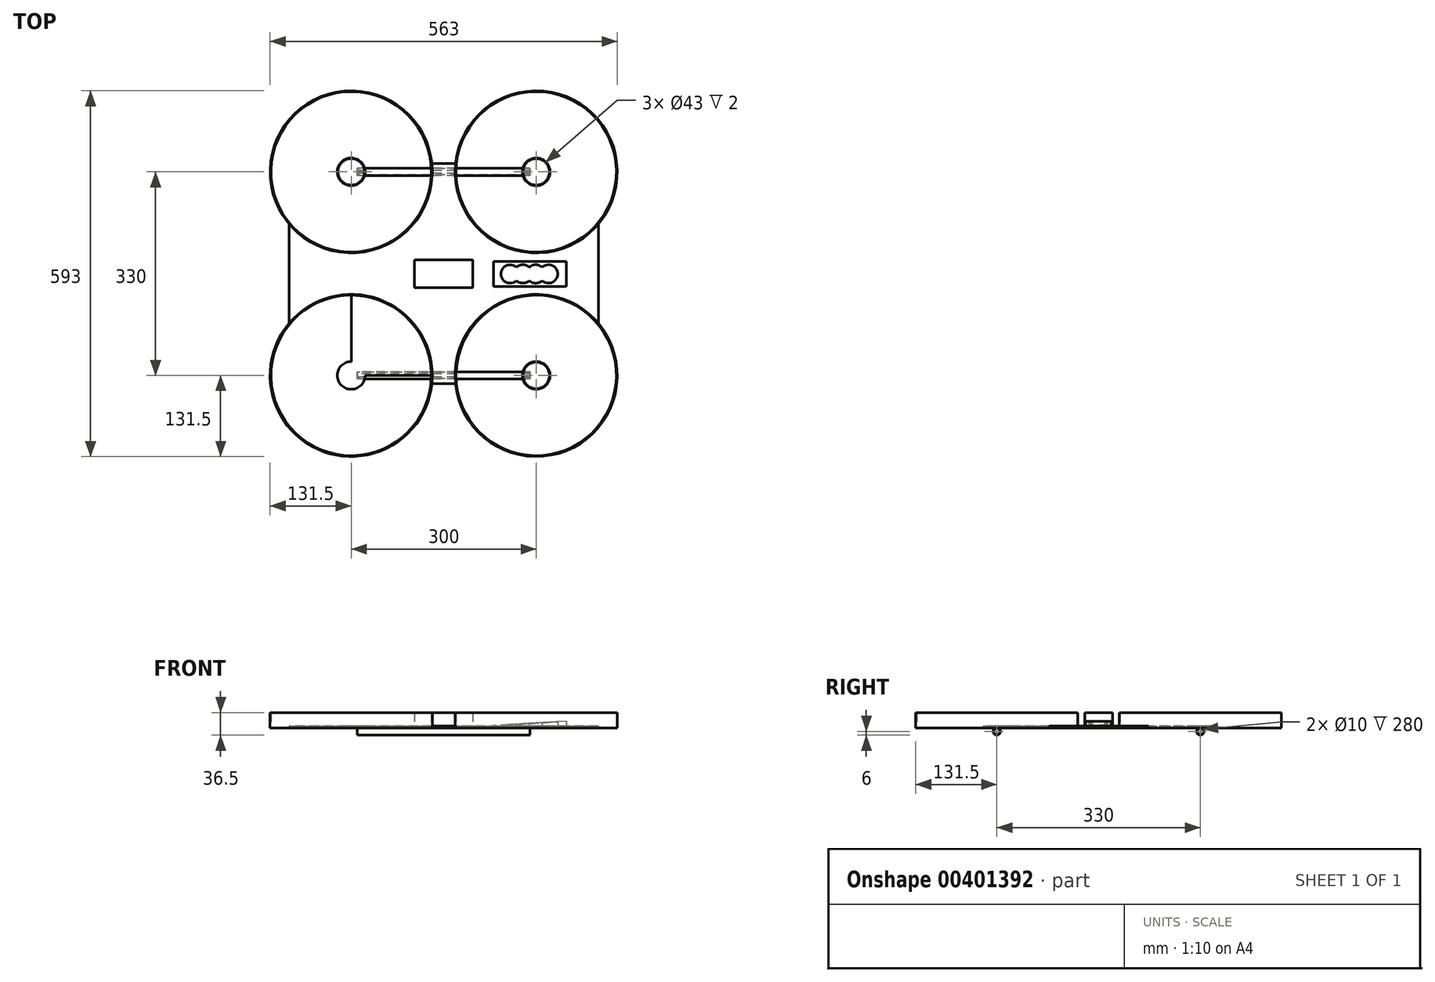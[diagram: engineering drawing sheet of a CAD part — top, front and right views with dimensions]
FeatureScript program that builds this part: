
annotation { "Feature Type Name" : "Feature", "Feature Type Description" : "" }
export const myFeature = defineFeature(function(context is Context, id is Id, definition is map)
    precondition{}
    {
        {
            var Q0;
            Q0=qCreatedBy(makeId("Top.planeOp"),FACE);
            var sketch = newSketch(context, id + "F0", { "sketchPlane" : qUnion([Q0])});
            skLineSegment(sketch, "E0.bottom", {"start": v(127.5, 165) * mm, "end": v(20, 165) * mm});
            skLineSegment(sketch, "E0.top", {"start": v(127.5, -165) * mm, "end": v(20, -165) * mm});
            skLineSegment(sketch, "E0.left", {"start": v(150, 142.5) * mm, "end": v(150, 35) * mm});
            skLineSegment(sketch, "E0.right", {"start": v(-150, 142.5) * mm, "end": v(-150, 35) * mm});
            skPoint(sketch, "E0.middle", {"position": v(0, 0) * mm});
            skArc(sketch, "E1", {"start": v(-277.12, 131.33) * mm, "mid": v(-136.22, 34.22) * mm, "end": v(-18.66, 158.56) * mm});
            skArc(sketch, "E2", {"start": v(-130.96, -295.11) * mm, "mid": v(-18.85, -155.46) * mm, "end": v(-150, -33.5) * mm});
            skArc(sketch, "E3", {"start": v(150, -33.5) * mm, "mid": v(140.46, -33.85) * mm, "end": v(130.96, -34.89) * mm});
            skArc(sketch, "E4", {"start": v(18.63, 159.26) * mm, "mid": v(135.88, 34.26) * mm, "end": v(277.12, 131.33) * mm});
            skArc(sketch, "E5", {"start": v(-150, 35) * mm, "mid": v(-60.39, 70.82) * mm, "end": v(-20.16, 158.55) * mm});
            skArc(sketch, "E6", {"start": v(-20.17, -158.32) * mm, "mid": v(-60.47, -70.74) * mm, "end": v(-150, -35) * mm});
            skArc(sketch, "E7", {"start": v(150, -35) * mm, "mid": v(60.47, -70.74) * mm, "end": v(20.17, -158.32) * mm});
            skArc(sketch, "E8", {"start": v(20.12, 159.3) * mm, "mid": v(60.11, 71.09) * mm, "end": v(150, 35) * mm});
            skArc(sketch, "E9", {"start": v(-127.5, 165) * mm, "mid": v(-165.9, 180.9) * mm, "end": v(-150, 142.5) * mm});
            skArc(sketch, "E10", {"start": v(172.44, 163.38) * mm, "mid": v(134.67, 181.47) * mm, "end": v(150, 142.5) * mm});
            skArc(sketch, "E11", {"start": v(150, -142.5) * mm, "mid": v(138.1, -184.1) * mm, "end": v(170.2, -155.1) * mm});
            skArc(sketch, "E12", {"start": v(-170.2, -155.1) * mm, "mid": v(-138.1, -184.1) * mm, "end": v(-150, -142.5) * mm});
            skPoint(sketch, "E13.orphan", {"position": v(-150, 179.73) * mm});
            skPoint(sketch, "E14.orphan", {"position": v(-171.77, 150.07) * mm});
            skArc(sketch, "E15.trimOffspring", {"start": v(-150, 33.5) * mm, "mid": v(-140.46, 33.85) * mm, "end": v(-130.96, 34.89) * mm});
            skLineSegment(sketch, "E16.trimOffspring", {"start": v(-150, 33.5) * mm, "end": v(-150, -33.5) * mm});
            skArc(sketch, "E17.trimOffspring", {"start": v(-150, 142.5) * mm, "mid": v(-141.54, 185.85) * mm, "end": v(-165.68, 148.86) * mm});
            skArc(sketch, "E18.trimOffspring", {"start": v(-20, 165) * mm, "mid": v(-241.92, 256.92) * mm, "end": v(-150, 35) * mm});
            skArc(sketch, "E19.trimOffspring", {"start": v(-18.5, 165) * mm, "mid": v(-242.98, 257.98) * mm, "end": v(-150, 33.5) * mm});
            skLineSegment(sketch, "E20.trimOffspring", {"start": v(-20, 165) * mm, "end": v(-127.5, 165) * mm});
            skLineSegment(sketch, "E21.trimOffspring", {"start": v(18.5, 165) * mm, "end": v(-18.5, 165) * mm});
            skPoint(sketch, "E22.orphan", {"position": v(150, 155.34) * mm});
            skArc(sketch, "E23.trimOffspring", {"start": v(150, 142.5) * mm, "mid": v(165.9, 180.9) * mm, "end": v(127.5, 165) * mm});
            skPoint(sketch, "E24.orphan", {"position": v(172.08, 149.08) * mm});
            skArc(sketch, "E25.trimOffspring", {"start": v(150, 35) * mm, "mid": v(241.92, 256.92) * mm, "end": v(20, 165) * mm});
            skArc(sketch, "E26.trimOffspring", {"start": v(150, 33.5) * mm, "mid": v(242.98, 257.98) * mm, "end": v(18.5, 165) * mm});
            skLineSegment(sketch, "E27.trimOffspring", {"start": v(150, 33.5) * mm, "end": v(150, -33.5) * mm});
            skLineSegment(sketch, "E28.trimOffspring", {"start": v(150, -35) * mm, "end": v(150, -142.5) * mm});
            skPoint(sketch, "E29.orphan", {"position": v(150, -179.73) * mm});
            skArc(sketch, "E30.trimOffspring", {"start": v(127.5, -165) * mm, "mid": v(165.9, -180.9) * mm, "end": v(150, -142.5) * mm});
            skPoint(sketch, "E31.orphan", {"position": v(171.77, -150.07) * mm});
            skArc(sketch, "E32.trimOffspring", {"start": v(277.12, -131.33) * mm, "mid": v(136.34, -34.21) * mm, "end": v(18.67, -158.33) * mm});
            skPoint(sketch, "E33.orphan", {"position": v(-171.77, -150.07) * mm});
            skArc(sketch, "E34.trimOffspring", {"start": v(130.97, 34.88) * mm, "mid": v(140.46, 33.85) * mm, "end": v(150, 33.5) * mm});
            skArc(sketch, "E35.trimOffspring", {"start": v(20, -165) * mm, "mid": v(241.92, -256.92) * mm, "end": v(150, -35) * mm});
            skLineSegment(sketch, "E36.trimOffspring", {"start": v(18.5, -165) * mm, "end": v(-18.5, -165) * mm});
            skArc(sketch, "E37.trimOffspring", {"start": v(18.5, -165) * mm, "mid": v(242.98, -257.98) * mm, "end": v(150, -33.5) * mm});
            skArc(sketch, "E38.trimOffspring", {"start": v(-18.67, -158.33) * mm, "mid": v(-136.34, -34.21) * mm, "end": v(-277.12, -131.33) * mm});
            skLineSegment(sketch, "E39.trimOffspring", {"start": v(-20, -165) * mm, "end": v(-127.5, -165) * mm});
            skPoint(sketch, "E40.orphan", {"position": v(-150, -155.34) * mm});
            skArc(sketch, "E41.trimOffspring", {"start": v(-150, -142.5) * mm, "mid": v(-165.9, -180.9) * mm, "end": v(-127.5, -165) * mm});
            skArc(sketch, "E42.trimOffspring", {"start": v(-150, -35) * mm, "mid": v(-241.92, -256.92) * mm, "end": v(-20, -165) * mm});
            skArc(sketch, "E43.trimOffspring", {"start": v(-150, -33.5) * mm, "mid": v(-242.98, -257.98) * mm, "end": v(-18.5, -165) * mm});
            skLineSegment(sketch, "E44.trimOffspring", {"start": v(-150, -35) * mm, "end": v(-150, -142.5) * mm});
            skArc(sketch, "E45", {"start": v(-20, -165) * mm, "mid": v(-20.06, -161.66) * mm, "end": v(-20.17, -158.32) * mm});
            skArc(sketch, "E46", {"start": v(20.17, -158.32) * mm, "mid": v(20.06, -161.66) * mm, "end": v(20, -165) * mm});
            skArc(sketch, "E47", {"start": v(18.67, -158.33) * mm, "mid": v(18.56, -161.66) * mm, "end": v(18.5, -165) * mm});
            skArc(sketch, "E48", {"start": v(-20.16, 158.55) * mm, "mid": v(-20.05, 161.77) * mm, "end": v(-20, 165) * mm});
            skArc(sketch, "E49", {"start": v(-18.66, 158.56) * mm, "mid": v(-18.55, 161.78) * mm, "end": v(-18.5, 165) * mm});
            skArc(sketch, "E50", {"start": v(18.5, 165) * mm, "mid": v(18.54, 162.13) * mm, "end": v(18.63, 159.26) * mm});
            skArc(sketch, "E51", {"start": v(20, 165) * mm, "mid": v(20.04, 162.15) * mm, "end": v(20.12, 159.3) * mm});
            skLineSegment(sketch, "E52.bottom", {"start": v(47.4, 22.5) * mm, "end": v(-47.6, 22.5) * mm});
            skLineSegment(sketch, "E52.top", {"start": v(47.4, -22.5) * mm, "end": v(-47.6, -22.5) * mm});
            skLineSegment(sketch, "E52.left", {"start": v(47.4, 22.5) * mm, "end": v(47.4, -22.5) * mm});
            skLineSegment(sketch, "E52.right", {"start": v(-47.6, 22.5) * mm, "end": v(-47.6, -22.5) * mm});
            skLineSegment(sketch, "E53.bottom", {"start": v(-56.8, 24.55) * mm, "end": v(-201.8, 24.55) * mm});
            skLineSegment(sketch, "E53.top", {"start": v(-56.8, -25.45) * mm, "end": v(-201.8, -25.45) * mm});
            skLineSegment(sketch, "E53.left", {"start": v(-56.8, 24.55) * mm, "end": v(-56.8, -25.45) * mm});
            skLineSegment(sketch, "E53.right", {"start": v(-201.8, 24.55) * mm, "end": v(-201.8, -25.45) * mm});
            skLineSegment(sketch, "E54", {"start": v(183.76, -0.32) * mm, "end": v(102.14, -0.5) * mm, "construction": true});
            skPoint(sketch, "E55.middle", {"position": v(128.38, -0.44) * mm});
            skPoint(sketch, "E56.middle", {"position": v(149.22, -0.4) * mm});
            skPoint(sketch, "E57.middle", {"position": v(170.04, -0.35) * mm});
            skPoint(sketch, "E58.oppositeSnap0", {"position": v(116.38, -9.4) * mm});
            skPoint(sketch, "E59.endSnap0", {"position": v(116.38, 12.6) * mm});
            skLineSegment(sketch, "E60", {"start": v(149.22, -0.4) * mm, "end": v(149.17, 22.64) * mm, "construction": true});
            skLineSegment(sketch, "E61", {"start": v(128.38, -0.44) * mm, "end": v(128.33, 20.3) * mm, "construction": true});
            skLineSegment(sketch, "E62", {"start": v(128.9, -13.3) * mm, "end": v(128.15, -13.3) * mm});
            skLineSegment(sketch, "E63", {"start": v(128.73, 12.53) * mm, "end": v(128.22, 12.53) * mm});
            skLineSegment(sketch, "E64", {"start": v(149.31, 12.87) * mm, "end": v(149.08, 12.87) * mm});
            skLineSegment(sketch, "E65", {"start": v(149.34, -13.69) * mm, "end": v(149.17, -13.69) * mm});
            skPoint(sketch, "E66.startSnap0", {"position": v(138.69, 8.5) * mm});
            skPoint(sketch, "E66.endSnap0", {"position": v(119, 9.26) * mm});
            skPoint(sketch, "E67.startSnap0", {"position": v(159.63, 8.54) * mm});
            skCircle(sketch, "E68", {"center": v(170.04, -0.35) * mm, "radius": 15 * mm});
            skCircle(sketch, "E69", {"center": v(107.6, -0.48) * mm, "radius": 15 * mm});
            skCircle(sketch, "E70", {"center": v(128.38, -0.44) * mm, "radius": 15 * mm});
            skCircle(sketch, "E71", {"center": v(149.16, -0.5) * mm, "radius": 15 * mm});
            skLineSegment(sketch, "E72.bottom", {"start": v(199, 20) * mm, "end": v(199, -21) * mm});
            skLineSegment(sketch, "E72.top", {"start": v(81, 20) * mm, "end": v(81, -21) * mm});
            skLineSegment(sketch, "E72.left", {"start": v(199, 20) * mm, "end": v(81, 20) * mm});
            skLineSegment(sketch, "E72.right", {"start": v(199, -21) * mm, "end": v(81, -21) * mm});
            skLineSegment(sketch, "E73", {"start": v(216.22, 51.4) * mm, "end": v(216.22, -51.4) * mm});
            skLineSegment(sketch, "E74", {"start": v(-215.9, 51.2) * mm, "end": v(-215.9, -51.2) * mm});
            skLineSegment(sketch, "E75", {"start": v(-19.2, 178.6) * mm, "end": v(19.2, 178.6) * mm});
            skLineSegment(sketch, "E76.MirrorCS", {"start": v(-19.2, -178.6) * mm, "end": v(19.2, -178.6) * mm});
            skLineSegment(sketch, "E77", {"start": v(250.68, 80.4) * mm, "end": v(250.68, -80.4) * mm});
            skLineSegment(sketch, "E78.MirrorCS", {"start": v(-250.68, 80.4) * mm, "end": v(-250.68, -80.4) * mm});
            skSolve(sketch);
        }
        {
            var Q0;
            {var subQ0=sQuery(id+"F0.wireOp",EDGE,"E16.trimOffspring");Q0=makeQuery(id+"F0.imprint","IMPRINT",FACE,{"disambiguationData":[TD([[makeQuery(id+"F0.imprint","IMPRINT",EDGE,{"derivedFrom":subQ0}),1.0]])]});}
            var Q1;
            {var subQ0=sQuery(id+"F0.wireOp",EDGE,"E27.trimOffspring");Q1=makeQuery(id+"F0.imprint","IMPRINT",FACE,{"disambiguationData":[TD([[makeQuery(id+"F0.imprint","IMPRINT",EDGE,{"derivedFrom":subQ0}),-1.0]])]});}
            var Q2;
            {var subQ0=sQuery(id+"F0.wireOp",EDGE,"E16.trimOffspring");Q2=makeQuery(id+"F0.imprint","IMPRINT",FACE,{"disambiguationData":[TD([[makeQuery(id+"F0.imprint","IMPRINT",EDGE,{"derivedFrom":subQ0}),1.0]])]});}
            var Q3;
            {var subQ0=sQuery(id+"F0.wireOp",EDGE,"E27.trimOffspring");Q3=makeQuery(id+"F0.imprint","IMPRINT",FACE,{"disambiguationData":[TD([[makeQuery(id+"F0.imprint","IMPRINT",EDGE,{"derivedFrom":subQ0}),-1.0]])]});}
            var Q4;
            {var subQ0=sQuery(id+"F0.wireOp",EDGE,"E44.trimOffspring");Q4=makeQuery(id+"F0.imprint","IMPRINT",FACE,{"disambiguationData":[TD([[makeQuery(id+"F0.imprint","IMPRINT",EDGE,{"derivedFrom":subQ0}),1.0]])]});}
            var Q5;
            {var subQ0=sQuery(id+"F0.wireOp",EDGE,"E16.trimOffspring");Q5=makeQuery(id+"F0.imprint","IMPRINT",FACE,{"disambiguationData":[TD([[makeQuery(id+"F0.imprint","IMPRINT",EDGE,{"derivedFrom":subQ0}),1.0]])]});}
            var Q6;
            {var subQ0=sQuery(id+"F0.wireOp",EDGE,"E41.trimOffspring");var subQ1=sQuery(id+"F0.wireOp",EDGE,"ztB0oHsk-U2iy-ewjn-oAiu-fDXbjUxa2sMx.top");var subQ2=makeQuery(id+"F0.imprint","INTERSECT",VERTEX,{"derivedFrom":[subQ1,subQ0]});Q6=makeQuery(id+"F0.imprint","IMPRINT",FACE,{"disambiguationData":[TD([[makeQuery(id+"F0.imprint","IMPRINT",EDGE,{"disambiguationData":[TD([[subQ2,-1.0]])],"derivedFrom":subQ1}),-1.0]])]});}
            var Q7;
            {var subQ0=sQuery(id+"F0.wireOp",EDGE,"E30.trimOffspring");var subQ3=sQuery(id+"F0.wireOp",EDGE,"5fd1df0c-a36e-472e-88ed-08a98f7d5a92.trimOffspring");var subQ5=makeQuery(id+"F0.imprint","INTERSECT",VERTEX,{"derivedFrom":[subQ0,subQ3]});Q7=makeQuery(id+"F0.imprint","IMPRINT",FACE,{"disambiguationData":[TD([[makeQuery(id+"F0.imprint","IMPRINT",EDGE,{"disambiguationData":[TD([[subQ5,1.0]])],"derivedFrom":subQ3}),-1.0]])]});}
            var Q8;
            {var subQ0=sQuery(id+"F0.wireOp",EDGE,"E41.trimOffspring");var subQ5=sQuery(id+"F0.wireOp",EDGE,"ztB0oHsk-U2iy-ewjn-oAiu-fDXbjUxa2sMx.top");var subQ7=makeQuery(id+"F0.imprint","INTERSECT",VERTEX,{"derivedFrom":[subQ5,subQ0]});Q8=makeQuery(id+"F0.imprint","IMPRINT",FACE,{"disambiguationData":[TD([[makeQuery(id+"F0.imprint","IMPRINT",EDGE,{"disambiguationData":[TD([[subQ7,-1.0]])],"derivedFrom":subQ5}),1.0]])]});}
            var Q9;
            Q9=makeQuery(id+"F0.imprint","IMPRINT",FACE,{"disambiguationData":[TD([[makeQuery(id+"F0.imprint","IMPRINT",EDGE,{"derivedFrom":sQuery(id+"F0.wireOp",EDGE,"694da14b-bd5c-4bf1-92a1-4cb310ea3b29.trimOffspring")}),1.0]])]});
            var Q10;
            Q10=makeQuery(id+"F0.imprint","IMPRINT",FACE,{"disambiguationData":[TD([[makeQuery(id+"F0.imprint","IMPRINT",EDGE,{"derivedFrom":sQuery(id+"F0.wireOp",EDGE,"E1")}),-1.0]])]});
            var Q11;
            {var subQ0=sQuery(id+"F0.wireOp",EDGE,"E2");Q11=makeQuery(id+"F0.imprint","IMPRINT",FACE,{"disambiguationData":[TD([[makeQuery(id+"F0.imprint","IMPRINT",EDGE,{"derivedFrom":subQ0}),-1.0]])]});}
            var Q12;
            {var subQ0=sQuery(id+"F0.wireOp",EDGE,"VxhCHl4m-0UAC-RpTz-ntCf-MOsYV9PffpKB");Q12=makeQuery(id+"F0.imprint","IMPRINT",FACE,{"disambiguationData":[TD([[makeQuery(id+"F0.imprint","IMPRINT",EDGE,{"derivedFrom":subQ0}),-1.0]])]});}
            var Q13;
            {var subQ0=sQuery(id+"F0.wireOp",EDGE,"BIsfn0BU-UTwV-kT4Y-hiiu-zm6SuCy18oyB.left");Q13=makeQuery(id+"F0.imprint","IMPRINT",FACE,{"disambiguationData":[TD([[makeQuery(id+"F0.imprint","IMPRINT",EDGE,{"derivedFrom":subQ0}),-1.0]])]});}
            var Q14;
            {var subQ0=sQuery(id+"F0.wireOp",EDGE,"E23.trimOffspring");var subQ3=sQuery(id+"F0.wireOp",EDGE,"5468dc64-bf4a-4afe-8942-5242e7b749a0.trimOffspring");var subQ5=makeQuery(id+"F0.imprint","INTERSECT",VERTEX,{"derivedFrom":[subQ3,subQ0]});Q14=makeQuery(id+"F0.imprint","IMPRINT",FACE,{"disambiguationData":[TD([[makeQuery(id+"F0.imprint","IMPRINT",EDGE,{"disambiguationData":[TD([[subQ5,1.0]])],"derivedFrom":subQ3}),1.0]])]});}
            var Q15;
            {var subQ0=sQuery(id+"F0.wireOp",EDGE,"E10");var subQ1=makeQuery(id+"F0.imprint","INTERSECT",VERTEX,{"derivedFrom":[subQ0,sQuery(id+"F0.wireOp",EDGE,"xMZpTOlw-Vo3L-Nwu6-rpHK-F8cbJvvAtKsT")]});Q15=makeQuery(id+"F0.imprint","IMPRINT",FACE,{"disambiguationData":[TD([[makeQuery(id+"F0.imprint","IMPRINT",EDGE,{"disambiguationData":[TD([[subQ1,1.0]])],"derivedFrom":subQ0}),1.0]])]});}
            var Q16;
            {var subQ0=sQuery(id+"F0.wireOp",EDGE,"E17.trimOffspring");var subQ4=makeQuery(id+"F0.imprint","INTERSECT",VERTEX,{"derivedFrom":[subQ0,sQuery(id+"F0.wireOp",EDGE,"E20.trimOffspring")]});Q16=makeQuery(id+"F0.imprint","IMPRINT",FACE,{"disambiguationData":[TD([[makeQuery(id+"F0.imprint","IMPRINT",EDGE,{"disambiguationData":[TD([[subQ4,1.0]])],"derivedFrom":subQ0}),1.0]])]});}
            var Q17;
            {var subQ1=sQuery(id+"F0.wireOp",EDGE,"E9");Q17=makeQuery(id+"F0.imprint","IMPRINT",FACE,{"disambiguationData":[TD([[makeQuery(id+"F0.imprint","IMPRINT",EDGE,{"derivedFrom":subQ1}),1.0]])]});}
            var Q18;
            {var subQ1=sQuery(id+"F0.wireOp",EDGE,"E11");var subQ5=makeQuery(id+"F0.imprint","INTERSECT",VERTEX,{"derivedFrom":[subQ1,sQuery(id+"F0.wireOp",EDGE,"xMZpTOlw-Vo3L-Nwu6-rpHK-F8cbJvvAtKsT")]});Q18=makeQuery(id+"F0.imprint","IMPRINT",FACE,{"disambiguationData":[TD([[makeQuery(id+"F0.imprint","IMPRINT",EDGE,{"disambiguationData":[TD([[subQ5,-1.0]])],"derivedFrom":subQ1}),1.0]])]});}
            var Q19;
            {var subQ1=sQuery(id+"F0.wireOp",EDGE,"E12");var subQ4=makeQuery(id+"F0.imprint","INTERSECT",VERTEX,{"derivedFrom":[subQ1,sQuery(id+"F0.wireOp",EDGE,"qoRHT7hJ-X9uN-FTaz-VIwN-q5ecVGCvl5hh")]});Q19=makeQuery(id+"F0.imprint","IMPRINT",FACE,{"disambiguationData":[TD([[makeQuery(id+"F0.imprint","IMPRINT",EDGE,{"disambiguationData":[TD([[subQ4,1.0]])],"derivedFrom":subQ1}),1.0]])]});}
            var Q20;
            Q20=makeQuery(id+"F0.imprint","IMPRINT",FACE,{"disambiguationData":[TD([[makeQuery(id+"F0.imprint","IMPRINT",EDGE,{"derivedFrom":sQuery(id+"F0.wireOp",EDGE,"E53.bottom")}),1.0]])]});
            var Q21;
            Q21=makeQuery(id+"F0.imprint","IMPRINT",FACE,{"disambiguationData":[TD([[makeQuery(id+"F0.imprint","IMPRINT",EDGE,{"derivedFrom":sQuery(id+"F0.wireOp",EDGE,"zMo2ETxv-PZvH-zb8n-VQOB-WDUzyCgouAGd.bottom")}),1.0]])]});
            var Q22;
            {var subQ5=sQuery(id+"F0.wireOp",EDGE,"E72.bottom");Q22=makeQuery(id+"F0.imprint","IMPRINT",FACE,{"disambiguationData":[TD([[makeQuery(id+"F0.imprint","IMPRINT",EDGE,{"derivedFrom":subQ5}),1.0]])]});}
            var Q23;
            {var subQ10=sQuery(id+"F0.wireOp",EDGE,"E53.right");Q23=makeQuery(id+"F0.imprint","IMPRINT",FACE,{"disambiguationData":[TD([[makeQuery(id+"F0.imprint","IMPRINT",EDGE,{"derivedFrom":subQ10}),-1.0]])]});}
            var Q24;
            {var subQ0=sQuery(id+"F0.wireOp",EDGE,"E74");Q24=makeQuery(id+"F0.imprint","IMPRINT",FACE,{"disambiguationData":[TD([[makeQuery(id+"F0.imprint","IMPRINT",EDGE,{"derivedFrom":subQ0}),-1.0]])]});}
            var Q25;
            {var subQ0=sQuery(id+"F0.wireOp",EDGE,"E36.trimOffspring");Q25=makeQuery(id+"F0.imprint","IMPRINT",FACE,{"disambiguationData":[TD([[makeQuery(id+"F0.imprint","IMPRINT",EDGE,{"derivedFrom":subQ0}),1.0]])]});}
            var Q26;
            {var subQ0=sQuery(id+"F0.wireOp",EDGE,"E73");Q26=makeQuery(id+"F0.imprint","IMPRINT",FACE,{"disambiguationData":[TD([[makeQuery(id+"F0.imprint","IMPRINT",EDGE,{"derivedFrom":subQ0}),1.0]])]});}
            var Q27;
            {var subQ0=sQuery(id+"F0.wireOp",EDGE,"E21.trimOffspring");Q27=makeQuery(id+"F0.imprint","IMPRINT",FACE,{"disambiguationData":[TD([[makeQuery(id+"F0.imprint","IMPRINT",EDGE,{"derivedFrom":subQ0}),-1.0]])]});}
            extrude(context, id + "F1", {"entities" : qUnion([Q0, Q1, Q2, Q3, Q4, Q5, Q6, Q7, Q8, Q9, Q10, Q11, Q12, Q13, Q14, Q15, Q16, Q17, Q18, Q19, Q20, Q21, Q22, Q23, Q24, Q25, Q26, Q27]), "depth" : 3 * mm});
        }
        {
            var Q0;
            Q0=makeQuery(id+"F1.opExtrude","CAP_FACE",FACE,{"disambiguationData":[OSD([sQuery(id+"F0.wireOp",EDGE,"E0.bottom"),sQuery(id+"F0.wireOp",EDGE,"E0.top"),sQuery(id+"F0.wireOp",EDGE,"E0.left"),sQuery(id+"F0.wireOp",EDGE,"E0.right"),sQuery(id+"F0.wireOp",EDGE,"E1"),sQuery(id+"F0.wireOp",EDGE,"E2"),sQuery(id+"F0.wireOp",EDGE,"E3"),sQuery(id+"F0.wireOp",EDGE,"E4"),sQuery(id+"F0.wireOp",EDGE,"E5"),sQuery(id+"F0.wireOp",EDGE,"E6"),sQuery(id+"F0.wireOp",EDGE,"E7"),sQuery(id+"F0.wireOp",EDGE,"E8"),sQuery(id+"F0.wireOp",EDGE,"BIsfn0BU-UTwV-kT4Y-hiiu-zm6SuCy18oyB.bottom"),sQuery(id+"F0.wireOp",EDGE,"BIsfn0BU-UTwV-kT4Y-hiiu-zm6SuCy18oyB.top"),sQuery(id+"F0.wireOp",EDGE,"BIsfn0BU-UTwV-kT4Y-hiiu-zm6SuCy18oyB.left"),sQuery(id+"F0.wireOp",EDGE,"BIsfn0BU-UTwV-kT4Y-hiiu-zm6SuCy18oyB.right"),sQuery(id+"F0.wireOp",EDGE,"ztB0oHsk-U2iy-ewjn-oAiu-fDXbjUxa2sMx.bottom"),sQuery(id+"F0.wireOp",EDGE,"ztB0oHsk-U2iy-ewjn-oAiu-fDXbjUxa2sMx.top"),sQuery(id+"F0.wireOp",EDGE,"E0.right"),sQuery(id+"F0.wireOp",EDGE,"E0.left"),sQuery(id+"F0.wireOp",EDGE,"E9"),sQuery(id+"F0.wireOp",EDGE,"E10"),sQuery(id+"F0.wireOp",EDGE,"E11"),sQuery(id+"F0.wireOp",EDGE,"E12"),sQuery(id+"F0.wireOp",EDGE,"E15.trimOffspring"),sQuery(id+"F0.wireOp",EDGE,"E16.trimOffspring"),sQuery(id+"F0.wireOp",EDGE,"E16.trimOffspring"),sQuery(id+"F0.wireOp",EDGE,"E17.trimOffspring"),sQuery(id+"F0.wireOp",EDGE,"E18.trimOffspring"),sQuery(id+"F0.wireOp",EDGE,"E19.trimOffspring"),sQuery(id+"F0.wireOp",EDGE,"E20.trimOffspring"),sQuery(id+"F0.wireOp",EDGE,"694da14b-bd5c-4bf1-92a1-4cb310ea3b29.trimOffspring"),sQuery(id+"F0.wireOp",EDGE,"E21.trimOffspring"),sQuery(id+"F0.wireOp",EDGE,"5468dc64-bf4a-4afe-8942-5242e7b749a0.trimOffspring"),sQuery(id+"F0.wireOp",EDGE,"E23.trimOffspring"),sQuery(id+"F0.wireOp",EDGE,"E25.trimOffspring"),sQuery(id+"F0.wireOp",EDGE,"E26.trimOffspring"),sQuery(id+"F0.wireOp",EDGE,"E27.trimOffspring"),sQuery(id+"F0.wireOp",EDGE,"E27.trimOffspring"),sQuery(id+"F0.wireOp",EDGE,"E28.trimOffspring"),sQuery(id+"F0.wireOp",EDGE,"E28.trimOffspring"),sQuery(id+"F0.wireOp",EDGE,"E30.trimOffspring"),sQuery(id+"F0.wireOp",EDGE,"E32.trimOffspring"),sQuery(id+"F0.wireOp",EDGE,"E34.trimOffspring"),sQuery(id+"F0.wireOp",EDGE,"E35.trimOffspring"),sQuery(id+"F0.wireOp",EDGE,"5fd1df0c-a36e-472e-88ed-08a98f7d5a92.trimOffspring"),sQuery(id+"F0.wireOp",EDGE,"E36.trimOffspring"),sQuery(id+"F0.wireOp",EDGE,"E37.trimOffspring"),sQuery(id+"F0.wireOp",EDGE,"E38.trimOffspring"),sQuery(id+"F0.wireOp",EDGE,"091660a7-41c7-4dc7-a4f7-27925c031a18.trimOffspring"),sQuery(id+"F0.wireOp",EDGE,"E39.trimOffspring"),sQuery(id+"F0.wireOp",EDGE,"E41.trimOffspring"),sQuery(id+"F0.wireOp",EDGE,"E42.trimOffspring"),sQuery(id+"F0.wireOp",EDGE,"E43.trimOffspring"),sQuery(id+"F0.wireOp",EDGE,"E44.trimOffspring"),sQuery(id+"F0.wireOp",EDGE,"E44.trimOffspring")])],"isStart":false});
            shell(context, id + "F2", {"entities" : qUnion([Q0]), "thickness" : 1 * mm});
        }
        {
            var Q0;
            {var subQ7=sQuery(id+"F0.wireOp",EDGE,"E1");Q0=makeQuery(id+"F0.imprint","IMPRINT",FACE,{"disambiguationData":[TD([[makeQuery(id+"F0.imprint","IMPRINT",EDGE,{"derivedFrom":subQ7}),1.0]])]});}
            var Q1;
            {var subQ10=sQuery(id+"F0.wireOp",EDGE,"E2");Q1=makeQuery(id+"F0.imprint","IMPRINT",FACE,{"disambiguationData":[TD([[makeQuery(id+"F0.imprint","IMPRINT",EDGE,{"derivedFrom":subQ10}),1.0]])]});}
            var Q2;
            {var subQ3=sQuery(id+"F0.wireOp",EDGE,"E38.trimOffspring");var subQ5=makeQuery(id+"F0.imprint","INTERSECT",VERTEX,{"derivedFrom":[subQ3,sQuery(id+"F0.wireOp",EDGE,"VxhCHl4m-0UAC-RpTz-ntCf-MOsYV9PffpKB")]});Q2=makeQuery(id+"F0.imprint","IMPRINT",FACE,{"disambiguationData":[TD([[makeQuery(id+"F0.imprint","IMPRINT",EDGE,{"disambiguationData":[TD([[subQ5,-1.0]])],"derivedFrom":subQ3}),1.0]])]});}
            var Q3;
            {var subQ5=sQuery(id+"F0.wireOp",EDGE,"E46");Q3=makeQuery(id+"F0.imprint","IMPRINT",FACE,{"disambiguationData":[TD([[makeQuery(id+"F0.imprint","IMPRINT",EDGE,{"derivedFrom":subQ5}),-1.0]])]});}
            var Q4;
            {var subQ0=sQuery(id+"F0.wireOp",EDGE,"E32.trimOffspring");var subQ1=makeQuery(id+"F0.imprint","INTERSECT",VERTEX,{"derivedFrom":[sQuery(id+"F0.wireOp",EDGE,"BIsfn0BU-UTwV-kT4Y-hiiu-zm6SuCy18oyB.left"),subQ0]});Q4=makeQuery(id+"F0.imprint","IMPRINT",FACE,{"disambiguationData":[TD([[makeQuery(id+"F0.imprint","IMPRINT",EDGE,{"disambiguationData":[TD([[subQ1,1.0]])],"derivedFrom":subQ0}),1.0]])]});}
            var Q5;
            {var subQ7=sQuery(id+"F0.wireOp",EDGE,"E4");Q5=makeQuery(id+"F0.imprint","IMPRINT",FACE,{"disambiguationData":[TD([[makeQuery(id+"F0.imprint","IMPRINT",EDGE,{"derivedFrom":subQ7}),1.0]])]});}
            var Q6;
            Q6=makeQuery(id+"F0.imprint","IMPRINT",FACE,{"disambiguationData":[TD([[makeQuery(id+"F0.imprint","IMPRINT",EDGE,{"derivedFrom":sQuery(id+"F0.wireOp",EDGE,"E52.bottom")}),1.0]])]});
            extrude(context, id + "F3", {"entities" : qUnion([Q0, Q1, Q2, Q3, Q4, Q5, Q6]), "operationType" : NewBodyOperationType.ADD, "depth" : 25 * mm});
        }
        {
            var Q0;
            Q0=qCreatedBy(makeId("Right.planeOp"),FACE);
            var sketch = newSketch(context, id + "F4", { "sketchPlane" : qUnion([Q0])});
            skCircle(sketch, "E79", {"center": v(-165, -5.5) * mm, "radius": 6 * mm});
            skCircle(sketch, "E80", {"center": v(-165, -5.5) * mm, "radius": 5 * mm});
            skCircle(sketch, "E81.MirrorC", {"center": v(165, -5.5) * mm, "radius": 6 * mm});
            skCircle(sketch, "E82.MirrorC", {"center": v(165, -5.5) * mm, "radius": 5 * mm});
            skSolve(sketch);
        }
        {
            var Q0;
            Q0=qSketchRegion(id+"F4",true);
            extrude(context, id + "F5", {"entities" : qUnion([Q0]), "operationType" : NewBodyOperationType.ADD, "endBound" : BoundingType.SYMMETRIC, "depth" : 280 * mm});
        }
        {
            var Q0;
            {var subQ7=sQuery(id+"F0.wireOp",EDGE,"E72.bottom");Q0=makeQuery(id+"F0.imprint","IMPRINT",FACE,{"disambiguationData":[TD([[makeQuery(id+"F0.imprint","IMPRINT",EDGE,{"derivedFrom":subQ7}),-1.0]])]});}
            var Q1;
            {var subQ14=sQuery(id+"F0.wireOp",EDGE,"E72.top");Q1=makeQuery(id+"F0.imprint","IMPRINT",FACE,{"disambiguationData":[TD([[makeQuery(id+"F0.imprint","IMPRINT",EDGE,{"derivedFrom":subQ14}),1.0]])]});}
            extrude(context, id + "F6", {"entities" : qUnion([Q0, Q1]), "operationType" : NewBodyOperationType.ADD, "depth" : 11 * mm});
        }
        {
            var Q0;
            Q0=makeQuery(id+"F6.opExtrude","CAP_EDGE",EDGE,{"disambiguationData":[OSD([sQuery(id+"F0.wireOp",EDGE,"E72.top")])],"isStart":false});
            chamfer(context, id + "F7", {"entities" : qUnion([Q0]), "chamferType" : ChamferType.TWO_OFFSETS, "width1" : 120 * mm, "oppositeDirection" : false, "width2" : 7 * mm, "tangentPropagation" : true});
        }
    });
